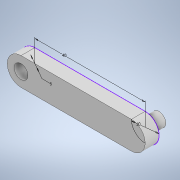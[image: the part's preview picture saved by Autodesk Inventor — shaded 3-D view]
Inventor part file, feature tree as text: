
AUTODESK INVENTOR PART (.ipt)
format: ipt  version: 2022 (Build 260153000, 153)  size: 108,544 bytes
history: native  units: mm
features: extrude x2, sketch x1
ambient origin geometry x8: Origin, YZ Plane, XZ Plane, XY Plane, X Axis, Y Axis, Z Axis, Center Point
bodies: Solid1 (feature_tree)
feature tree (3):
  sketch  "Sketch1"  dims[d0=10.0mm d1=5.0mm d2=40.0mm d3=5.0mm d4=0.0mm d5=5.0mm d6=0.0mm]
  extrude  "Extrusion1"  Depth=5.0mm
  extrude  "Extrusion2"  Depth=5.0mm
